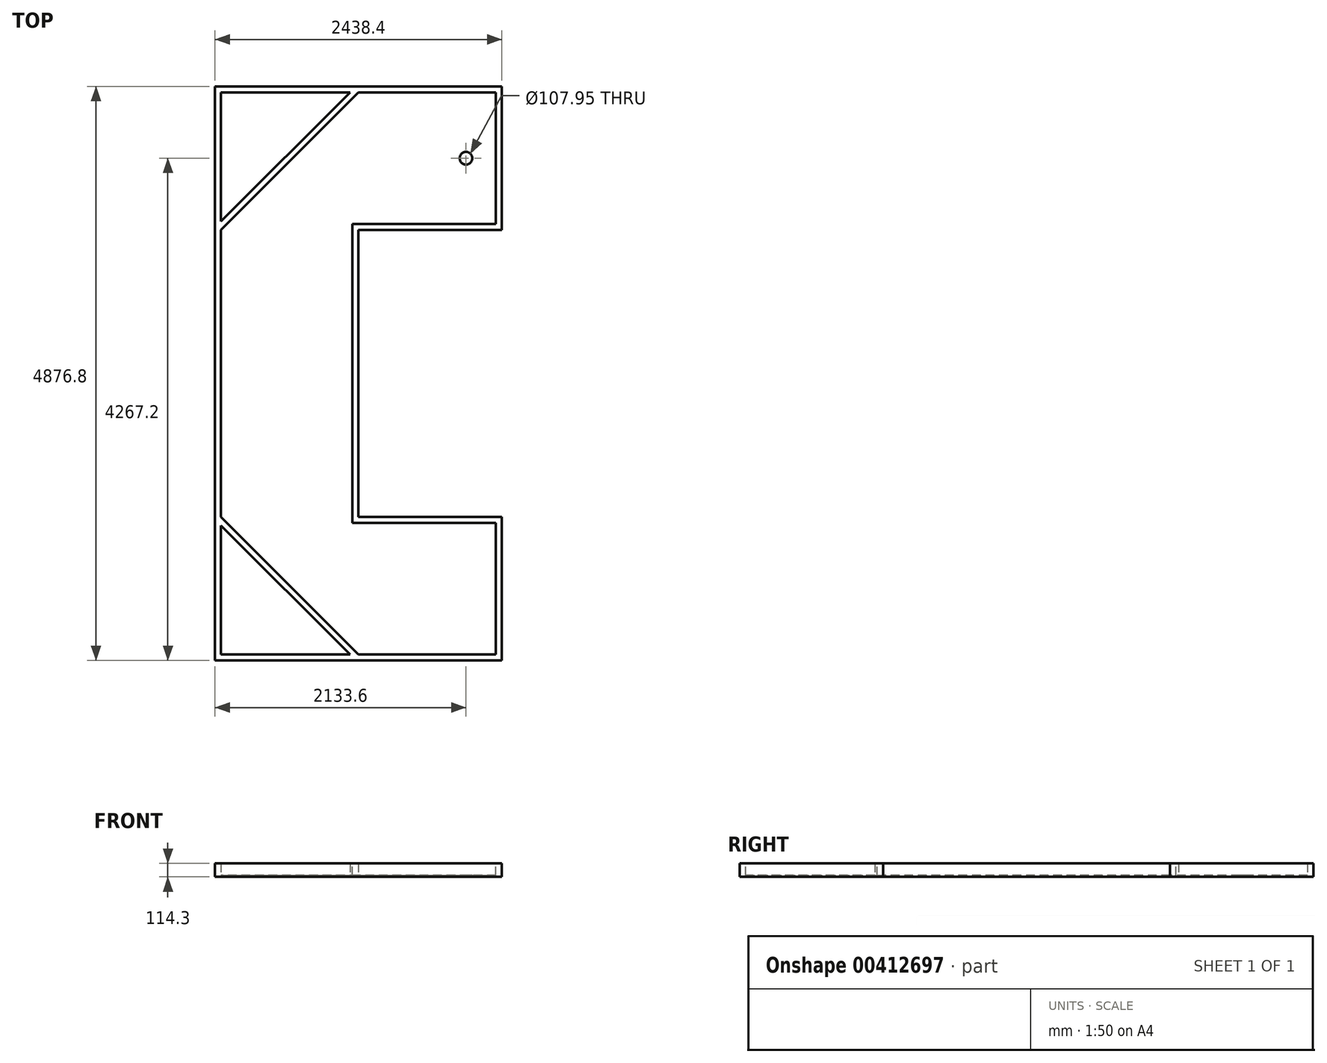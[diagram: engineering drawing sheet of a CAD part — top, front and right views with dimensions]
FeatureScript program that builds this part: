
annotation { "Feature Type Name" : "Feature", "Feature Type Description" : "" }
export const myFeature = defineFeature(function(context is Context, id is Id, definition is map)
    precondition{}
    {
        {
            var Q0;
            Q0=qCreatedBy(makeId("Top.planeOp"),FACE);
            var sketch = newSketch(context, id + "F0", { "sketchPlane" : qUnion([Q0])});
            skLineSegment(sketch, "E0", {"start": v(0, 0) * mm, "end": v(2438.4, 0) * mm});
            skLineSegment(sketch, "E1", {"start": v(2438.4, 0) * mm, "end": v(2438.4, 1219.2) * mm});
            skLineSegment(sketch, "E2", {"start": v(2438.4, 1219.2) * mm, "end": v(1219.2, 1219.2) * mm});
            skLineSegment(sketch, "E3", {"start": v(1219.2, 1219.2) * mm, "end": v(1219.2, 3657.6) * mm});
            skLineSegment(sketch, "E4", {"start": v(1219.2, 3657.6) * mm, "end": v(2438.4, 3657.6) * mm});
            skLineSegment(sketch, "E5", {"start": v(2438.4, 3657.6) * mm, "end": v(2438.4, 4876.8) * mm});
            skLineSegment(sketch, "E6", {"start": v(2438.4, 4876.8) * mm, "end": v(0, 4876.8) * mm});
            skLineSegment(sketch, "E7", {"start": v(0, 4876.8) * mm, "end": v(0, 0) * mm});
            skSolve(sketch);
        }
        {
            var Q0;
            Q0 = qSketchRegion(id + "F0", true);
            extrude(context, id + "F1", {"entities" : qUnion([Q0]), "depth" : 114.3 * mm});
        }
        {
            var Q0;
            Q0=makeQuery(id+"F1.opExtrude","CAP_FACE",FACE,{"disambiguationData":[OSD([sQuery(id+"F0.wireOp",EDGE,"E0"),sQuery(id+"F0.wireOp",EDGE,"E1"),sQuery(id+"F0.wireOp",EDGE,"E2"),sQuery(id+"F0.wireOp",EDGE,"E3"),sQuery(id+"F0.wireOp",EDGE,"E4"),sQuery(id+"F0.wireOp",EDGE,"E5"),sQuery(id+"F0.wireOp",EDGE,"E6"),sQuery(id+"F0.wireOp",EDGE,"E7")])],"isStart":false});
            var sketch = newSketch(context, id + "F2", { "sketchPlane" : qUnion([Q0])});
            skLineSegment(sketch, "E8", {"start": v(50.8, 4826) * mm, "end": v(50.8, 50.8) * mm});
            skLineSegment(sketch, "E9", {"start": v(50.8, 50.8) * mm, "end": v(2387.6, 50.8) * mm});
            skLineSegment(sketch, "E10", {"start": v(2387.6, 50.8) * mm, "end": v(2387.6, 1168.4) * mm});
            skLineSegment(sketch, "E11", {"start": v(2387.6, 1168.4) * mm, "end": v(1168.4, 1168.4) * mm});
            skLineSegment(sketch, "E12", {"start": v(1168.4, 1168.4) * mm, "end": v(1168.4, 3708.4) * mm});
            skLineSegment(sketch, "E13", {"start": v(1168.4, 3708.4) * mm, "end": v(2387.6, 3708.4) * mm});
            skLineSegment(sketch, "E14", {"start": v(50.8, 4826) * mm, "end": v(2387.6, 4826) * mm});
            skLineSegment(sketch, "E15", {"start": v(2387.6, 4826) * mm, "end": v(2387.6, 3708.4) * mm});
            skSolve(sketch);
        }
        {
            var Q0;
            Q0 = qSketchRegion(id + "F2", true);
            extrude(context, id + "F3", {"entities" : qUnion([Q0]), "operationType" : NewBodyOperationType.REMOVE, "oppositeDirection" : true, "depth" : 101.6 * mm});
        }
        {
            var Q0;
            Q0=makeQuery(id+"F3.boolean.opBoolean","COPY",FACE,{"derivedFrom":makeQuery(id+"F3.opExtrude","CAP_FACE",FACE,{"disambiguationData":[OSD([sQuery(id+"F2.wireOp",EDGE,"E8"),sQuery(id+"F2.wireOp",EDGE,"E9"),sQuery(id+"F2.wireOp",EDGE,"E10"),sQuery(id+"F2.wireOp",EDGE,"E11"),sQuery(id+"F2.wireOp",EDGE,"E12"),sQuery(id+"F2.wireOp",EDGE,"E13"),sQuery(id+"F2.wireOp",EDGE,"E14"),sQuery(id+"F2.wireOp",EDGE,"E15")])],"isStart":false})});
            var sketch = newSketch(context, id + "F4", { "sketchPlane" : qUnion([Q0])});
            skCircle(sketch, "E16", {"center": v(2133.6, 4267.2) * mm, "radius": 53.98 * mm});
            skSolve(sketch);
        }
        {
            var Q0;
            Q0 = qSketchRegion(id + "F4", true);
            extrude(context, id + "F5", {"entities" : qUnion([Q0]), "operationType" : NewBodyOperationType.REMOVE, "oppositeDirection" : true, "depth" : 12.7 * mm});
        }
        {
            var Q0;
            Q0=makeQuery(id+"F3.boolean.opBoolean","COPY",FACE,{"derivedFrom":makeQuery(id+"F3.opExtrude","CAP_FACE",FACE,{"disambiguationData":[OSD([sQuery(id+"F2.wireOp",EDGE,"E8"),sQuery(id+"F2.wireOp",EDGE,"E9"),sQuery(id+"F2.wireOp",EDGE,"E10"),sQuery(id+"F2.wireOp",EDGE,"E11"),sQuery(id+"F2.wireOp",EDGE,"E12"),sQuery(id+"F2.wireOp",EDGE,"E13"),sQuery(id+"F2.wireOp",EDGE,"E14"),sQuery(id+"F2.wireOp",EDGE,"E15")])],"isStart":false})});
            var sketch = newSketch(context, id + "F6", { "sketchPlane" : qUnion([Q0])});
            skLineSegment(sketch, "E17", {"start": v(50.8, 3729.44) * mm, "end": v(1147.36, 4826) * mm});
            skLineSegment(sketch, "E18", {"start": v(1147.36, 4826) * mm, "end": v(1219.2, 4826) * mm});
            skLineSegment(sketch, "E19", {"start": v(1219.2, 4826) * mm, "end": v(50.8, 3657.6) * mm});
            skLineSegment(sketch, "E20", {"start": v(50.8, 3657.6) * mm, "end": v(50.8, 3729.44) * mm});
            skLineSegment(sketch, "E21", {"start": v(1168.4, 2438.4) * mm, "end": v(50.8, 2438.4) * mm, "construction": true});
            skLineSegment(sketch, "E22.MirrorCS", {"start": v(1147.36, 50.8) * mm, "end": v(1219.2, 50.8) * mm});
            skLineSegment(sketch, "E23.MirrorCS", {"start": v(50.8, 1219.2) * mm, "end": v(50.8, 1147.36) * mm});
            skLineSegment(sketch, "E24.MirrorCS", {"start": v(1219.2, 50.8) * mm, "end": v(50.8, 1219.2) * mm});
            skLineSegment(sketch, "E25.MirrorCS", {"start": v(50.8, 1147.36) * mm, "end": v(1147.36, 50.8) * mm});
            skSolve(sketch);
        }
        {
            var Q0;
            Q0 = qSketchRegion(id + "F6", true);
            extrude(context, id + "F7", {"entities" : qUnion([Q0]), "operationType" : NewBodyOperationType.ADD, "depth" : 101.6 * mm});
        }
    });
